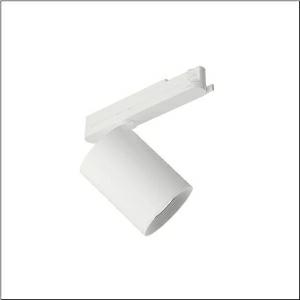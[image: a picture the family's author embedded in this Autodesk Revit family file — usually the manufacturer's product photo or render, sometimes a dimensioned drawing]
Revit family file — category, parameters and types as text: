
# Revit family: spot_21_51se14mbb5b
name_source: partatom
category: Lighting Fixtures
units: mm (PartAtom-declared; Revit-internal decimal feet)

## family parameters
Cut with Voids When Loaded = No
Host = Face
Light Source = No
Part Type = Normal
Room Calculation Point = No
Round Connector Dimension = Use Diameter
Shared = No

## types (1)
- --- (1 x LED, 5530 lm, 41.8 W, 3000K)
    Apparent Load = 42 VA
    CIE Flux Codes = 96 99 100 100 100
    Color Rendering = 90
    Color Temperature = 3000K
    Default Elevation = 1800 mm
    Description = Spot 21, directional spotlight, light control with lens, of PMMA, LED rated luminous flux: 5.110lm, light colour: 930, control gear: ECG Multilumen, with 3-phase adapter, mains connection: 220..240V, AC, 50/60Hz, of aluminium, traffic white (RAL 9016), length: 213mm, diameter: 105mm, protection rating (complete): IP20, insulation class (complete): insulation class I (protective earthing), certification: CE, impact resistance: IK02, permissible ambient temperature for indoor applications: -20..+40°C, packaging unit: 1 piece
    Height = 175 mm
    Lamp = 1 x LED
    Lamp Light Flux = 5530 lm
    Lamp Power = 41.8 W
    Lamp count = 1
    Length = 105 mm
    Luminous efficacy = 132 lm/W
    Manufacturer = Siteco
    ModVariant = No
    Model = 51SE14MBB5B
    Mounting Place = Ceiling
    Mounting Type = Pendant
    Number of Poles = 1
    OnlyDefault = Yes
    Power Factor = 1
    Product Name = Spot 21
    Product group = directional spotlight
    ProductGroupID = 905
    Protection Class = Protection class I
    Protection Degree = IP 20
    RLX_Detail_Level = 1
    RLX_Emergency_Light_Flux = 0 lm
    RLX_Emergency_Type = 0
    RLX_Emergency_Type_DB = No
    RlxData = <blob elided: 17665 chars, md5=bb2a4f7e>
    Socket = socket
    Standby Power = 0 W
    System Light Flux = 5530 lm
    System Power = 42 W
    Type Comments = factory setting: luminous flux: 100 % | (ON | ON | ON | ON) | 1050 mA
    Type Image = l_1003976.jpg
    URL = http://relux.com
    VarID = @adj_165121
    Voltage = 0 V
    Weight = 0.00 kg
    Width = 0 mm  [stored 0 ft]

note: [stored X ft] marks values corroborated as IEEE doubles in the binary element streams (Revit-internal decimal feet)

## geometry (parser evidence)
native form markers: Blend x4, Sweep x11
no freeform markers — native parametric forms only
